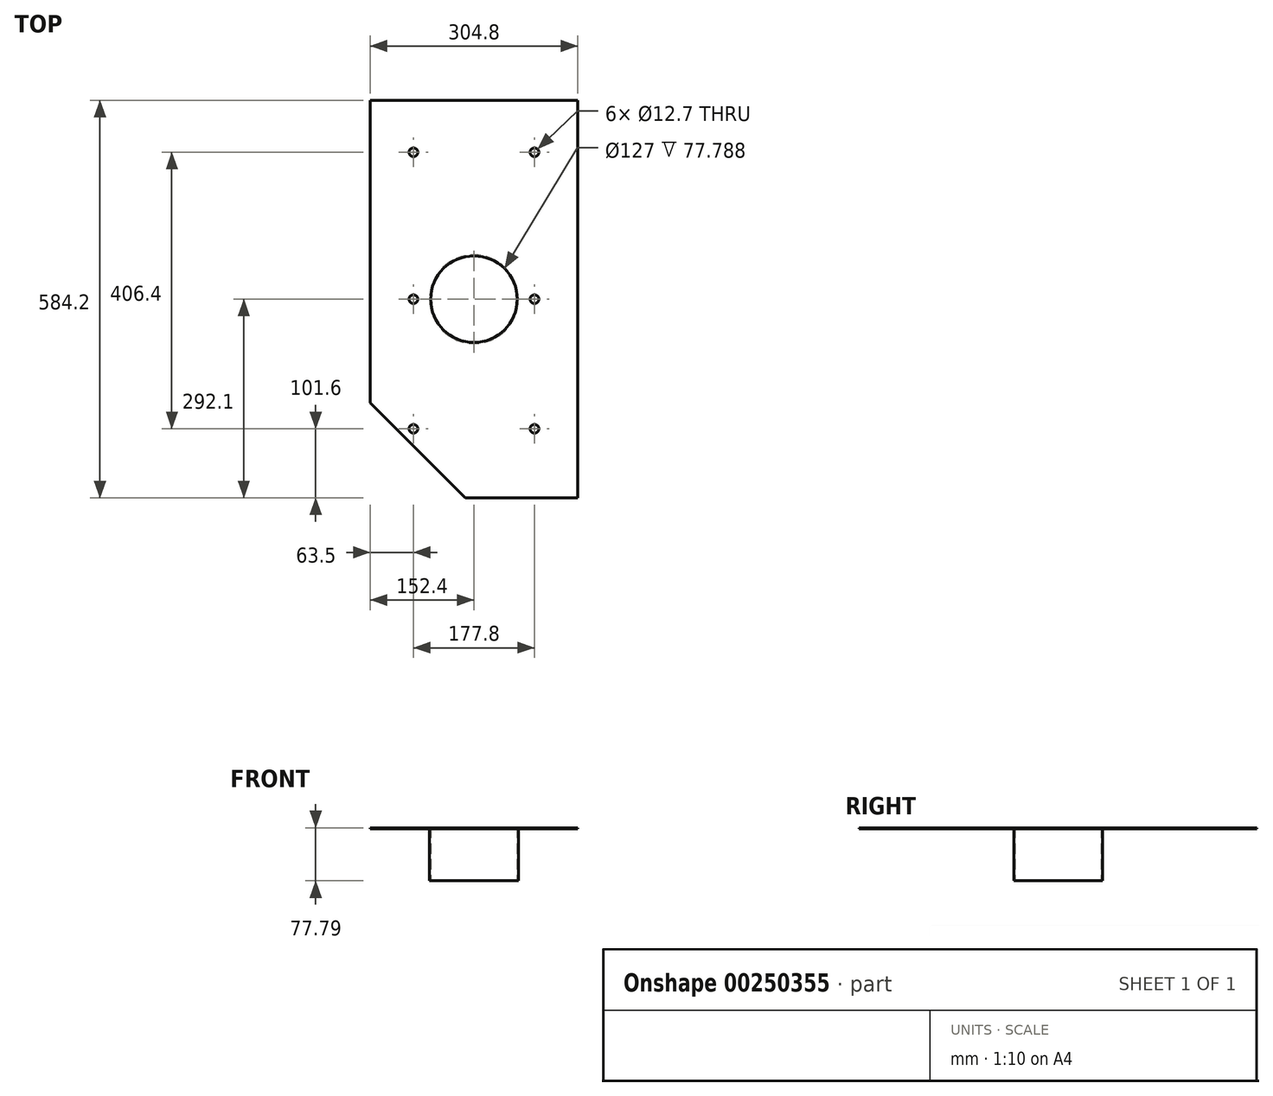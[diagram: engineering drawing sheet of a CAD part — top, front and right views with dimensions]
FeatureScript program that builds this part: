
annotation { "Feature Type Name" : "Feature", "Feature Type Description" : "" }
export const myFeature = defineFeature(function(context is Context, id is Id, definition is map)
    precondition{}
    {
        {
            var Q0;
            Q0=qCreatedBy(makeId("Top.planeOp"),FACE);
            var sketch = newSketch(context, id + "F0", { "sketchPlane" : qUnion([Q0])});
            skLineSegment(sketch, "E0.bottom", {"start": v(152.4, 292.1) * mm, "end": v(-152.4, 292.1) * mm});
            skLineSegment(sketch, "E0.top", {"start": v(12.7, -292.1) * mm, "end": v(-12.7, -292.1) * mm});
            skLineSegment(sketch, "E0.left", {"start": v(152.4, 292.1) * mm, "end": v(152.4, -152.4) * mm});
            skLineSegment(sketch, "E0.right", {"start": v(-152.4, 292.1) * mm, "end": v(-152.4, -152.4) * mm});
            skPoint(sketch, "E0.middle", {"position": v(0, 0) * mm});
            skCircle(sketch, "E1", {"center": v(0, 0) * mm, "radius": 63.5 * mm});
            skPoint(sketch, "E2.orphan", {"position": v(152.4, -292.1) * mm});
            skLineSegment(sketch, "E3", {"start": v(12.7, -292.1) * mm, "end": v(152.4, -292.1) * mm});
            skLineSegment(sketch, "E4", {"start": v(152.4, -152.4) * mm, "end": v(152.4, -292.1) * mm});
            skLineSegment(sketch, "E5", {"start": v(-152.4, -152.4) * mm, "end": v(-12.7, -292.1) * mm});
            skPoint(sketch, "E6.orphan", {"position": v(-152.4, -292.1) * mm});
            skLineSegment(sketch, "E7", {"start": v(-88.9, 292.1) * mm, "end": v(-88.9, -215.9) * mm});
            skLineSegment(sketch, "E8", {"start": v(-88.9, -215.9) * mm, "end": v(-88.9, 222.25) * mm});
            skLineSegment(sketch, "E9", {"start": v(88.9, 292.1) * mm, "end": v(88.9, -292.1) * mm});
            skLineSegment(sketch, "E10", {"start": v(88.9, -292.1) * mm, "end": v(88.9, 292.1) * mm});
            skLineSegment(sketch, "E11", {"start": v(-152.4, 215.9) * mm, "end": v(-82.55, 215.9) * mm});
            skLineSegment(sketch, "E12", {"start": v(152.4, -190.5) * mm, "end": v(82.55, -190.5) * mm});
            skCircle(sketch, "E13", {"center": v(-88.9, 215.9) * mm, "radius": 6.35 * mm});
            skCircle(sketch, "E14", {"center": v(88.9, 215.9) * mm, "radius": 6.35 * mm});
            skCircle(sketch, "E15", {"center": v(-88.9, -190.5) * mm, "radius": 6.35 * mm});
            skCircle(sketch, "E16", {"center": v(88.9, -190.5) * mm, "radius": 6.35 * mm});
            skLineSegment(sketch, "E17.trimOffspring", {"start": v(82.55, 215.9) * mm, "end": v(152.4, 215.9) * mm});
            skLineSegment(sketch, "E18.trimOffspring", {"start": v(-82.55, -190.5) * mm, "end": v(-114.3, -190.5) * mm});
            skLineSegment(sketch, "E19", {"start": v(152.4, -190.5) * mm, "end": v(-114.3, -190.5) * mm});
            skLineSegment(sketch, "E20", {"start": v(-152.4, -152.4) * mm, "end": v(-152.4, -292.1) * mm});
            skCircle(sketch, "E21", {"center": v(-88.9, 0) * mm, "radius": 6.35 * mm});
            skCircle(sketch, "E22", {"center": v(88.9, 0) * mm, "radius": 6.35 * mm});
            skSolve(sketch);
        }
        {
            var Q0;
            Q0=qSketchRegion(id+"F0",true);
            extrude(context, id + "F1", {"entities" : qUnion([Q0]), "depth" : 1.59 * mm});
        }
        {
            var Q0;
            Q0=makeQuery(id+"F1.opExtrude","CAP_FACE",FACE,{"disambiguationData":[OSD([sQuery(id+"F0.wireOp",EDGE,"E0.bottom"),sQuery(id+"F0.wireOp",EDGE,"E0.top"),sQuery(id+"F0.wireOp",EDGE,"E0.left"),sQuery(id+"F0.wireOp",EDGE,"E0.right"),sQuery(id+"F0.wireOp",EDGE,"E1")])],"isStart":true});
            var sketch = newSketch(context, id + "F2", { "sketchPlane" : qUnion([Q0])});
            skCircle(sketch, "E23", {"center": v(0, 0) * mm, "radius": 63.5 * mm});
            skCircle(sketch, "E24", {"center": v(0, 0) * mm, "radius": 65.09 * mm});
            skSolve(sketch);
        }
        {
            var Q0;
            Q0=qSketchRegion(id+"F2",true);
            extrude(context, id + "F3", {"entities" : qUnion([Q0]), "operationType" : NewBodyOperationType.ADD, "depth" : 76.2 * mm});
        }
    });
